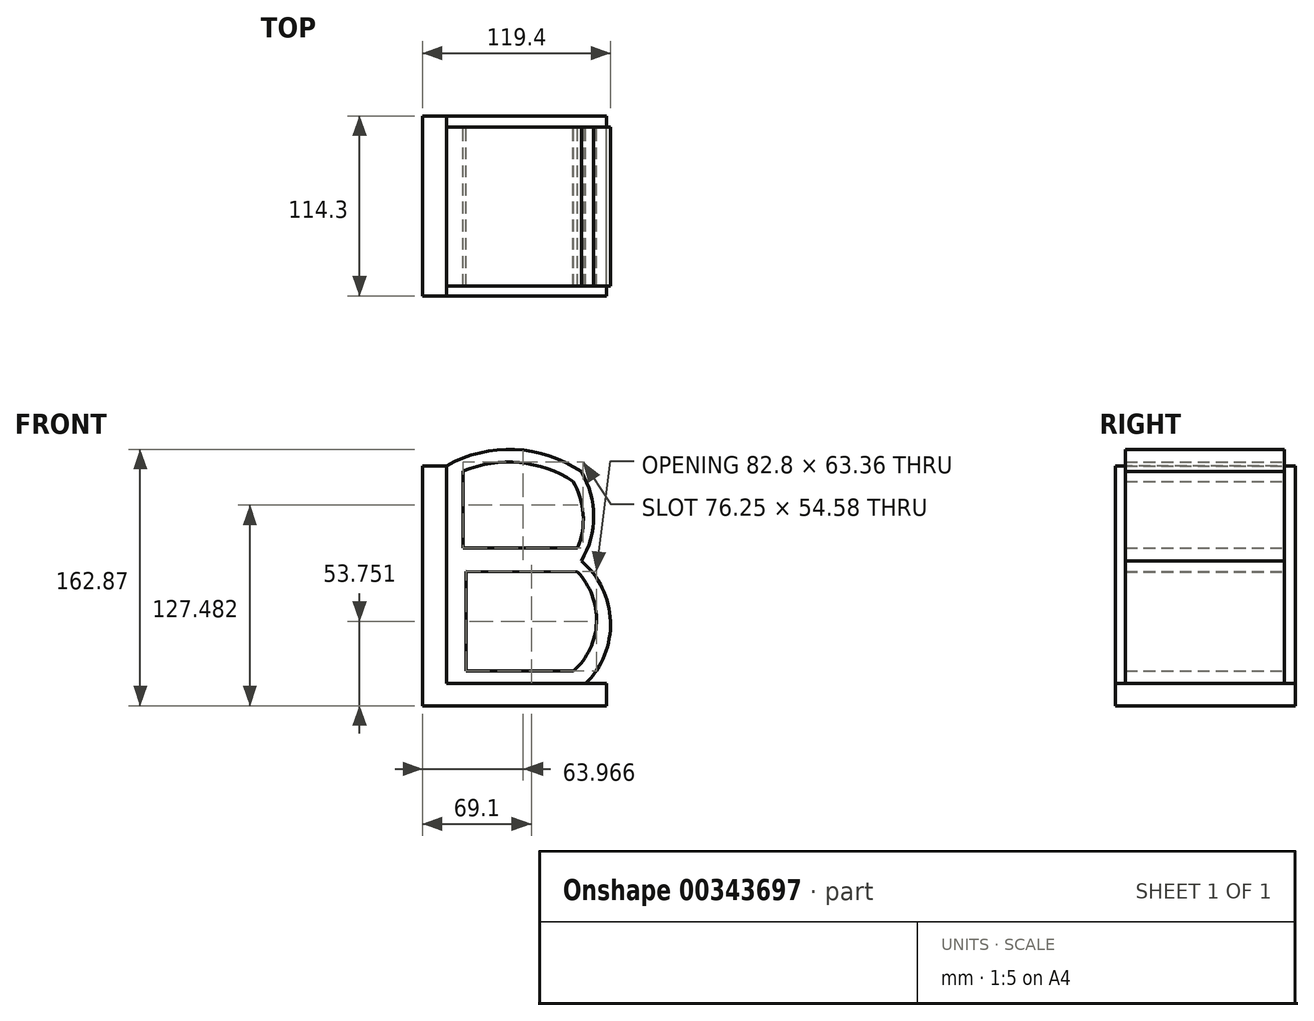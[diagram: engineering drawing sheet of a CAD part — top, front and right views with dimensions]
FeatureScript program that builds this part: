
annotation { "Feature Type Name" : "Feature", "Feature Type Description" : "" }
export const myFeature = defineFeature(function(context is Context, id is Id, definition is map)
    precondition{}
    {
        {
            var Q0;
            Q0=qCreatedBy(makeId("Right.planeOp"),FACE);
            var sketch = newSketch(context, id + "F0", { "sketchPlane" : qUnion([Q0])});
            skLineSegment(sketch, "E0.bottom", {"start": v(57.15, -76.2) * mm, "end": v(-57.15, -76.2) * mm});
            skLineSegment(sketch, "E0.top", {"start": v(57.15, 76.2) * mm, "end": v(-57.15, 76.2) * mm});
            skLineSegment(sketch, "E0.left", {"start": v(57.15, -76.2) * mm, "end": v(57.15, 76.2) * mm});
            skLineSegment(sketch, "E0.right", {"start": v(-57.15, -76.2) * mm, "end": v(-57.15, 76.2) * mm});
            skPoint(sketch, "E0.middle", {"position": v(0, 0) * mm});
            skSolve(sketch);
        }
        {
            var Q0;
            Q0 = qSketchRegion(id + "F0", true);
            extrude(context, id + "F1", {"entities" : qUnion([Q0]), "depth" : 15.24 * mm});
        }
        {
            var Q0;
            Q0=qCreatedBy(makeId("Front.planeOp"),FACE);
            var sketch = newSketch(context, id + "F2", { "sketchPlane" : qUnion([Q0])});
            skLineSegment(sketch, "E1.bottom", {"start": v(15.24, -76.2) * mm, "end": v(116.84, -76.2) * mm});
            skLineSegment(sketch, "E1.top", {"start": v(15.24, -62.09) * mm, "end": v(116.84, -62.09) * mm});
            skLineSegment(sketch, "E1.left", {"start": v(15.24, -76.2) * mm, "end": v(15.24, -62.09) * mm});
            skLineSegment(sketch, "E1.right", {"start": v(116.84, -76.2) * mm, "end": v(116.84, -62.09) * mm});
            skSolve(sketch);
        }
        {
            var Q0;
            Q0 = qSketchRegion(id + "F2", true);
            extrude(context, id + "F3", {"entities" : qUnion([Q0]), "operationType" : NewBodyOperationType.ADD, "depth" : 57.15 * mm});
        }
        {
            var Q0;
            Q0 = qSketchRegion(id + "F2", true);
            extrude(context, id + "F4", {"entities" : qUnion([Q0]), "operationType" : NewBodyOperationType.ADD, "oppositeDirection" : true, "depth" : 57.15 * mm});
        }
        {
            var Q0;
            Q0=qCreatedBy(makeId("Front.planeOp"),FACE);
            var sketch = newSketch(context, id + "F5", { "sketchPlane" : qUnion([Q0])});
            skArc(sketch, "E2", {"start": v(100.9, 72.53) * mm, "mid": v(58.6, 86.6) * mm, "end": v(15.24, 76.2) * mm});
            skArc(sketch, "E3", {"start": v(100.9, 15.83) * mm, "mid": v(108.74, 44.18) * mm, "end": v(100.9, 72.53) * mm});
            skArc(sketch, "E4", {"start": v(103.5, -62.09) * mm, "mid": v(119.37, -22.56) * mm, "end": v(100.9, 15.83) * mm});
            skLineSegment(sketch, "E5", {"start": v(27.7, 9.23) * mm, "end": v(27.7, -54.13) * mm});
            skLineSegment(sketch, "E6", {"start": v(27.7, -54.13) * mm, "end": v(95.98, -54.13) * mm});
            skArc(sketch, "E7", {"start": v(95.98, -54.13) * mm, "mid": v(110.5, -23.12) * mm, "end": v(98.44, 8.92) * mm});
            skLineSegment(sketch, "E8", {"start": v(98.44, 8.92) * mm, "end": v(27.7, 9.23) * mm});
            skArc(sketch, "E9", {"start": v(98.44, 24) * mm, "mid": v(102.05, 45.54) * mm, "end": v(95.66, 66.44) * mm});
            skArc(sketch, "E10", {"start": v(95.66, 66.44) * mm, "mid": v(61.55, 78.28) * mm, "end": v(25.84, 72.9) * mm});
            skLineSegment(sketch, "E11", {"start": v(25.84, 72.9) * mm, "end": v(25.84, 24) * mm});
            skLineSegment(sketch, "E12", {"start": v(25.84, 24) * mm, "end": v(98.44, 24) * mm});
            skLineSegment(sketch, "E13", {"start": v(15.24, 76.2) * mm, "end": v(15.24, -63.75) * mm});
            skLineSegment(sketch, "E14.0", {"start": v(15.24, -62.09) * mm, "end": v(116.84, -62.09) * mm});
            skSolve(sketch);
        }
        {
            var Q0;
            {var subQ0=sQuery(id+"F5.wireOp",EDGE,"E2");Q0=makeQuery(id+"F5.imprint","IMPRINT",FACE,{"disambiguationData":[TD([[makeQuery(id+"F5.imprint","IMPRINT",EDGE,{"derivedFrom":subQ0}),1.0]])]});}
            extrude(context, id + "F6", {"entities" : qUnion([Q0]), "operationType" : NewBodyOperationType.ADD, "depth" : 50.8 * mm});
        }
        {
            var Q0;
            Q0=makeQuery(id+"F6.opExtrude","CAP_FACE",FACE,{"disambiguationData":[OSD([sQuery(id+"F5.wireOp",EDGE,"E2"),sQuery(id+"F5.wireOp",EDGE,"E3"),sQuery(id+"F5.wireOp",EDGE,"E4"),sQuery(id+"F5.wireOp",EDGE,"E5"),sQuery(id+"F5.wireOp",EDGE,"E6"),sQuery(id+"F5.wireOp",EDGE,"E7"),sQuery(id+"F5.wireOp",EDGE,"E8"),sQuery(id+"F5.wireOp",EDGE,"E9"),sQuery(id+"F5.wireOp",EDGE,"E10"),sQuery(id+"F5.wireOp",EDGE,"E11"),sQuery(id+"F5.wireOp",EDGE,"E12"),sQuery(id+"F5.wireOp",EDGE,"E13"),sQuery(id+"F5.wireOp",EDGE,"E14.0")])],"isStart":false});
            extrude(context, id + "F7", {"entities" : qUnion([Q0]), "operationType" : NewBodyOperationType.ADD, "oppositeDirection" : true, "depth" : 100.84 * mm});
        }
    });
